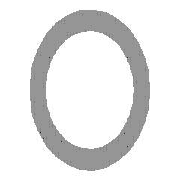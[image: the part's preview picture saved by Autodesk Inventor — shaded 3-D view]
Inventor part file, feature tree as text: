
AUTODESK INVENTOR PART (.ipt)
format: ipt  version: 2013 (Build 170138000, 138)  size: 113,152 bytes
history: native  units: mm (DEFAULTED — no unit token found)
features: other x4, sketch x3, plane x2, split x1
ambient origin geometry x8: Origin, YZ Plane, XZ Plane, XY Plane, X Axis, Y Axis, Z Axis, Center Point
bodies: Solid1 (feature_tree), Body (feature_tree)
feature tree (10):
  parser-record x1  (decoder bookkeeping rows leaked as tree rows — omitted from the tree; the rows remain in map.json)
  other  "Driven Length"
  other  "Start plane"
  other  "End plane"
  plane  "Work Plane4"
  split  "Split1"
  sketch  "Sketch"  dims[d2=541.401mm d3=0.0mm d4=-0.0mm d5=541.401mm d6=90.0deg d7=541.401mm]
  sketch  "Sketch3"  dims[d0=33.401mm]
  plane  "Work Plane3"
  sketch  "Sketch4"  dims[d1=3.3782mm]
